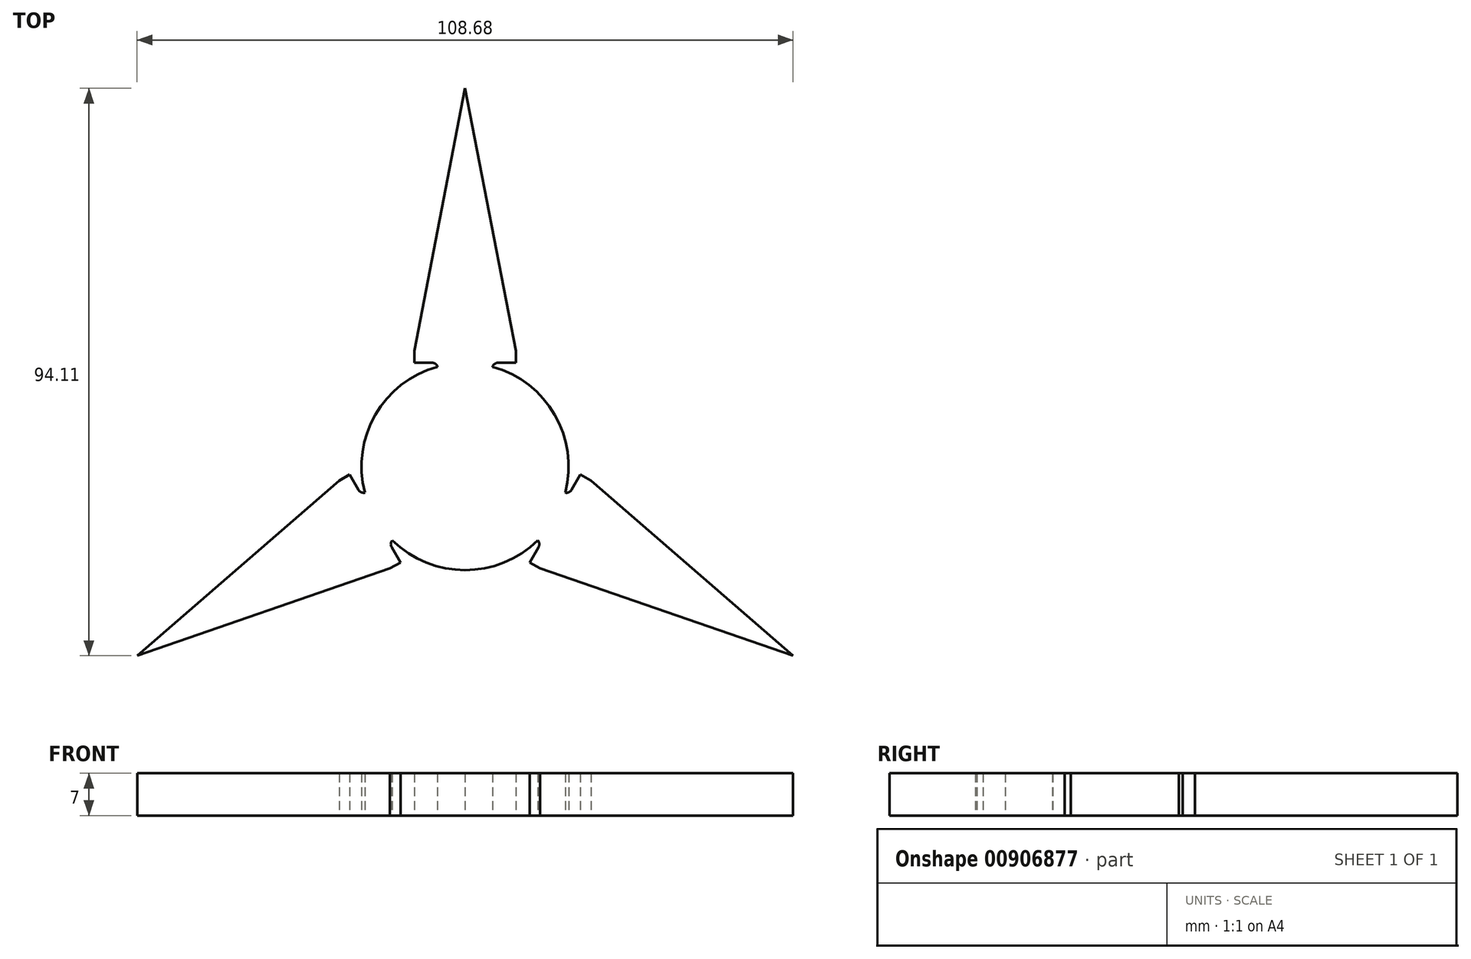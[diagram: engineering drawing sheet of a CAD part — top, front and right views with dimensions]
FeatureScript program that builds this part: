
annotation { "Feature Type Name" : "Feature", "Feature Type Description" : "" }
export const myFeature = defineFeature(function(context is Context, id is Id, definition is map)
    precondition{}
    {
        {
            var Q0;
            Q0=qCreatedBy(makeId("Top.planeOp"),FACE);
            var sketch = newSketch(context, id + "F0", { "sketchPlane" : qUnion([Q0])});
            skCircle(sketch, "E0", {"center": v(0, 0) * mm, "radius": 10.9 * mm});
            skLineSegment(sketch, "E1", {"start": v(-5.5, 17.22) * mm, "end": v(-8.4, 17.22) * mm});
            skLineSegment(sketch, "E2", {"start": v(-8.4, 17.22) * mm, "end": v(-8.4, 19.22) * mm});
            skLineSegment(sketch, "E3", {"start": v(-8.4, 19.22) * mm, "end": v(0, 62.74) * mm});
            skPoint(sketch, "E4.visualSharp", {"position": v(-4.5, 17.22) * mm});
            skArc(sketch, "E4.filletArc", {"start": v(-4.55, 16.55) * mm, "mid": v(-4.92, 17.04) * mm, "end": v(-5.5, 17.22) * mm});
            skLineSegment(sketch, "E5.MirrorCS", {"start": v(8.4, 19.22) * mm, "end": v(0, 62.74) * mm});
            skLineSegment(sketch, "E6.MirrorCS", {"start": v(8.4, 17.22) * mm, "end": v(8.4, 19.22) * mm});
            skLineSegment(sketch, "E7.MirrorCS", {"start": v(5.5, 17.22) * mm, "end": v(8.4, 17.22) * mm});
            skPoint(sketch, "E8.MirrorP", {"position": v(4.5, 17.22) * mm});
            skArc(sketch, "E9.MirrorCS", {"start": v(4.55, 16.55) * mm, "mid": v(4.92, 17.04) * mm, "end": v(5.5, 17.22) * mm});
            skLineSegment(sketch, "E10.1.0", {"start": v(-20.85, -2.33) * mm, "end": v(-54.34, -31.37) * mm});
            skPoint(sketch, "E10.1.1", {"position": v(-17.17, -4.72) * mm});
            skPoint(sketch, "E10.1.4", {"position": v(-12.67, -12.5) * mm});
            skLineSegment(sketch, "E10.1.5", {"start": v(-12.44, -16.89) * mm, "end": v(-54.34, -31.37) * mm});
            skArc(sketch, "E10.1.6", {"start": v(-16.3, -4.22) * mm, "mid": v(-17.06, -4.32) * mm, "end": v(-17.67, -3.85) * mm});
            skLineSegment(sketch, "E10.1.7", {"start": v(-10.71, -15.9) * mm, "end": v(-12.44, -16.89) * mm});
            skLineSegment(sketch, "E10.1.8", {"start": v(-12.17, -13.37) * mm, "end": v(-10.71, -15.9) * mm});
            skLineSegment(sketch, "E10.1.9", {"start": v(-19.12, -1.33) * mm, "end": v(-20.85, -2.33) * mm});
            skLineSegment(sketch, "E10.1.10", {"start": v(-17.67, -3.85) * mm, "end": v(-19.12, -1.33) * mm});
            skArc(sketch, "E10.1.11", {"start": v(-11.8, -12) * mm, "mid": v(-12.27, -12.62) * mm, "end": v(-12.17, -13.37) * mm});
            skLineSegment(sketch, "E10.2.0", {"start": v(12.44, -16.89) * mm, "end": v(54.34, -31.37) * mm});
            skPoint(sketch, "E10.2.1", {"position": v(12.67, -12.5) * mm});
            skPoint(sketch, "E10.2.4", {"position": v(17.17, -4.72) * mm});
            skLineSegment(sketch, "E10.2.5", {"start": v(20.85, -2.33) * mm, "end": v(54.34, -31.37) * mm});
            skArc(sketch, "E10.2.6", {"start": v(11.8, -12) * mm, "mid": v(12.27, -12.62) * mm, "end": v(12.17, -13.37) * mm});
            skLineSegment(sketch, "E10.2.7", {"start": v(19.12, -1.33) * mm, "end": v(20.85, -2.33) * mm});
            skLineSegment(sketch, "E10.2.8", {"start": v(17.67, -3.85) * mm, "end": v(19.12, -1.33) * mm});
            skLineSegment(sketch, "E10.2.9", {"start": v(10.71, -15.9) * mm, "end": v(12.44, -16.89) * mm});
            skLineSegment(sketch, "E10.2.10", {"start": v(12.17, -13.37) * mm, "end": v(10.71, -15.9) * mm});
            skArc(sketch, "E10.2.11", {"start": v(16.3, -4.22) * mm, "mid": v(17.06, -4.32) * mm, "end": v(17.67, -3.85) * mm});
            skCircle(sketch, "E11.cCircle", {"center": v(0, 24.39) * mm, "radius": 5.45 * mm, "construction": true});
            skLineSegment(sketch, "E11.0", {"start": v(3.15, 18.94) * mm, "end": v(-3.15, 18.94) * mm});
            skLineSegment(sketch, "E11.1", {"start": v(-3.15, 18.94) * mm, "end": v(-6.3, 24.39) * mm});
            skLineSegment(sketch, "E11.2", {"start": v(-6.3, 24.39) * mm, "end": v(-3.15, 29.84) * mm});
            skLineSegment(sketch, "E11.3", {"start": v(-3.15, 29.84) * mm, "end": v(3.15, 29.84) * mm});
            skLineSegment(sketch, "E11.4", {"start": v(3.15, 29.84) * mm, "end": v(6.3, 24.39) * mm});
            skLineSegment(sketch, "E11.5", {"start": v(6.3, 24.39) * mm, "end": v(3.15, 18.94) * mm});
            skPoint(sketch, "E11.0.midPoint", {"position": v(0, 18.94) * mm});
            skLineSegment(sketch, "E12.1.0", {"start": v(-27.41, -12.2) * mm, "end": v(-24.27, -6.74) * mm});
            skLineSegment(sketch, "E12.1.1", {"start": v(-24.27, -17.64) * mm, "end": v(-27.41, -12.2) * mm});
            skLineSegment(sketch, "E12.1.2", {"start": v(-17.97, -17.64) * mm, "end": v(-24.27, -17.64) * mm});
            skLineSegment(sketch, "E12.1.3", {"start": v(-14.83, -12.2) * mm, "end": v(-17.97, -17.64) * mm});
            skLineSegment(sketch, "E12.1.4", {"start": v(-17.97, -6.74) * mm, "end": v(-14.83, -12.2) * mm});
            skLineSegment(sketch, "E12.1.5", {"start": v(-24.27, -6.74) * mm, "end": v(-17.97, -6.74) * mm});
            skLineSegment(sketch, "E12.2.0", {"start": v(24.27, -17.64) * mm, "end": v(17.97, -17.64) * mm});
            skLineSegment(sketch, "E12.2.1", {"start": v(27.41, -12.2) * mm, "end": v(24.27, -17.64) * mm});
            skLineSegment(sketch, "E12.2.2", {"start": v(24.27, -6.74) * mm, "end": v(27.41, -12.2) * mm});
            skLineSegment(sketch, "E12.2.3", {"start": v(17.97, -6.74) * mm, "end": v(24.27, -6.74) * mm});
            skLineSegment(sketch, "E12.2.4", {"start": v(14.83, -12.2) * mm, "end": v(17.97, -6.74) * mm});
            skLineSegment(sketch, "E12.2.5", {"start": v(17.97, -17.64) * mm, "end": v(14.83, -12.2) * mm});
            skCircle(sketch, "E13", {"center": v(0, 0) * mm, "radius": 17.17 * mm});
            skPoint(sketch, "E14.orphan", {"position": v(-4.5, 16.22) * mm});
            skPoint(sketch, "E15.orphan", {"position": v(4.5, 16.22) * mm});
            skSolve(sketch);
        }
        {
            var Q0;
            Q0 = qSketchRegion(id + "F0", true);
            var Q1;
            Q1=makeQuery(id+"F0.imprint","IMPRINT",FACE,{"disambiguationData":[TD([[makeQuery(id+"F0.imprint","IMPRINT",EDGE,{"derivedFrom":sQuery(id+"F0.wireOp",EDGE,"E11.0")}),-1.0]])]});
            var Q2;
            Q2=makeQuery(id+"F0.imprint","IMPRINT",FACE,{"disambiguationData":[TD([[makeQuery(id+"F0.imprint","IMPRINT",EDGE,{"derivedFrom":sQuery(id+"F0.wireOp",EDGE,"E12.1.0")}),-1.0]])]});
            var Q3;
            Q3=makeQuery(id+"F0.imprint","IMPRINT",FACE,{"disambiguationData":[TD([[makeQuery(id+"F0.imprint","IMPRINT",EDGE,{"derivedFrom":sQuery(id+"F0.wireOp",EDGE,"E0")}),1.0]])]});
            var Q4;
            Q4=makeQuery(id+"F0.imprint","IMPRINT",FACE,{"disambiguationData":[TD([[makeQuery(id+"F0.imprint","IMPRINT",EDGE,{"derivedFrom":sQuery(id+"F0.wireOp",EDGE,"E12.2.0")}),-1.0]])]});
            extrude(context, id + "F1", {"entities" : qUnion([Q0, Q1, Q2, Q3, Q4]), "depth" : 7 * mm, "offsetDistance" : 25 * mm});
        }
    });
